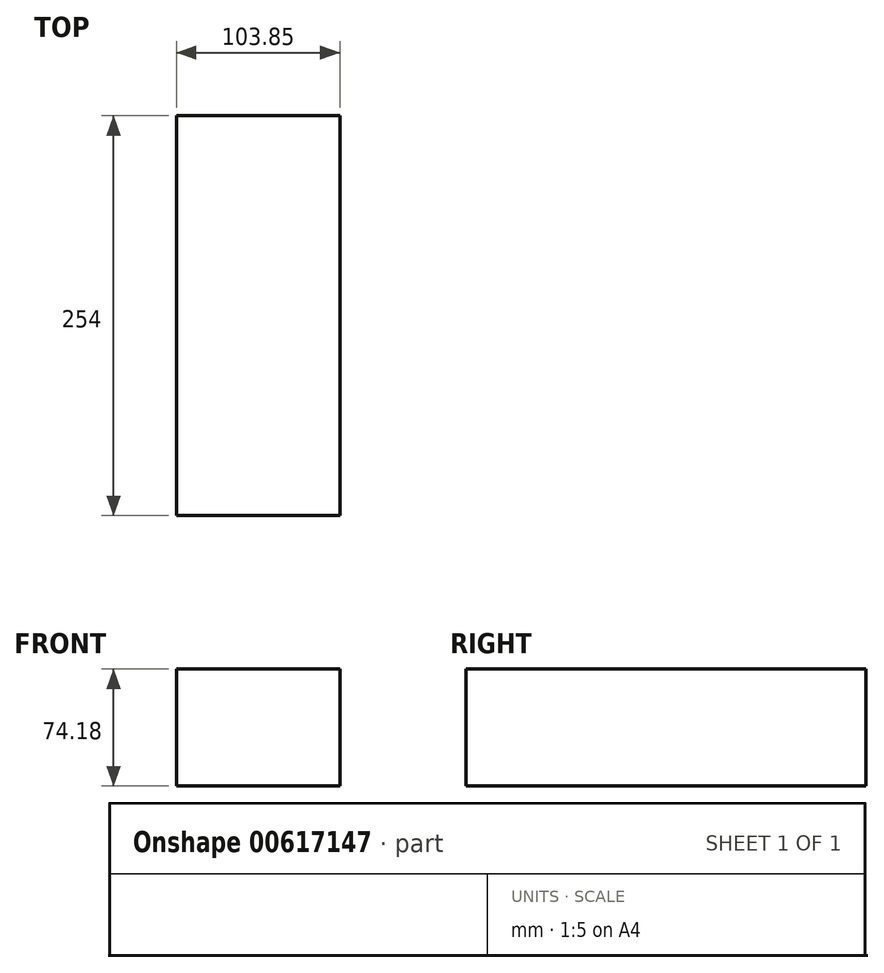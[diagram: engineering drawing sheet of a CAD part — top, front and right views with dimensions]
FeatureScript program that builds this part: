
annotation { "Feature Type Name" : "Feature", "Feature Type Description" : "" }
export const myFeature = defineFeature(function(context is Context, id is Id, definition is map)
    precondition{}
    {
        {
            var Q0;
            Q0=qCreatedBy(makeId("Front.planeOp"),FACE);
            var sketch = newSketch(context, id + "F0", { "sketchPlane" : qUnion([Q0])});
            skLineSegment(sketch, "E0.bottom", {"start": v(-36.57, 42.54) * mm, "end": v(67.28, 42.54) * mm});
            skLineSegment(sketch, "E0.top", {"start": v(-36.57, -31.64) * mm, "end": v(67.28, -31.64) * mm});
            skLineSegment(sketch, "E0.left", {"start": v(-36.57, 42.54) * mm, "end": v(-36.57, -31.64) * mm});
            skLineSegment(sketch, "E0.right", {"start": v(67.28, 42.54) * mm, "end": v(67.28, -31.64) * mm});
            skSolve(sketch);
        }
        {
            var Q0;
            Q0=makeQuery(id+"F0.imprint","IMPRINT",FACE,{"disambiguationData":[TD([[makeQuery(id+"F0.imprint","IMPRINT",EDGE,{"derivedFrom":sQuery(id+"F0.wireOp",EDGE,"E0.bottom")}),-1.0]])]});
            extrude(context, id + "F1", {"entities" : qUnion([Q0]), "depth" : 254 * mm, "offsetDistance" : 25.4 * mm});
        }
    });
